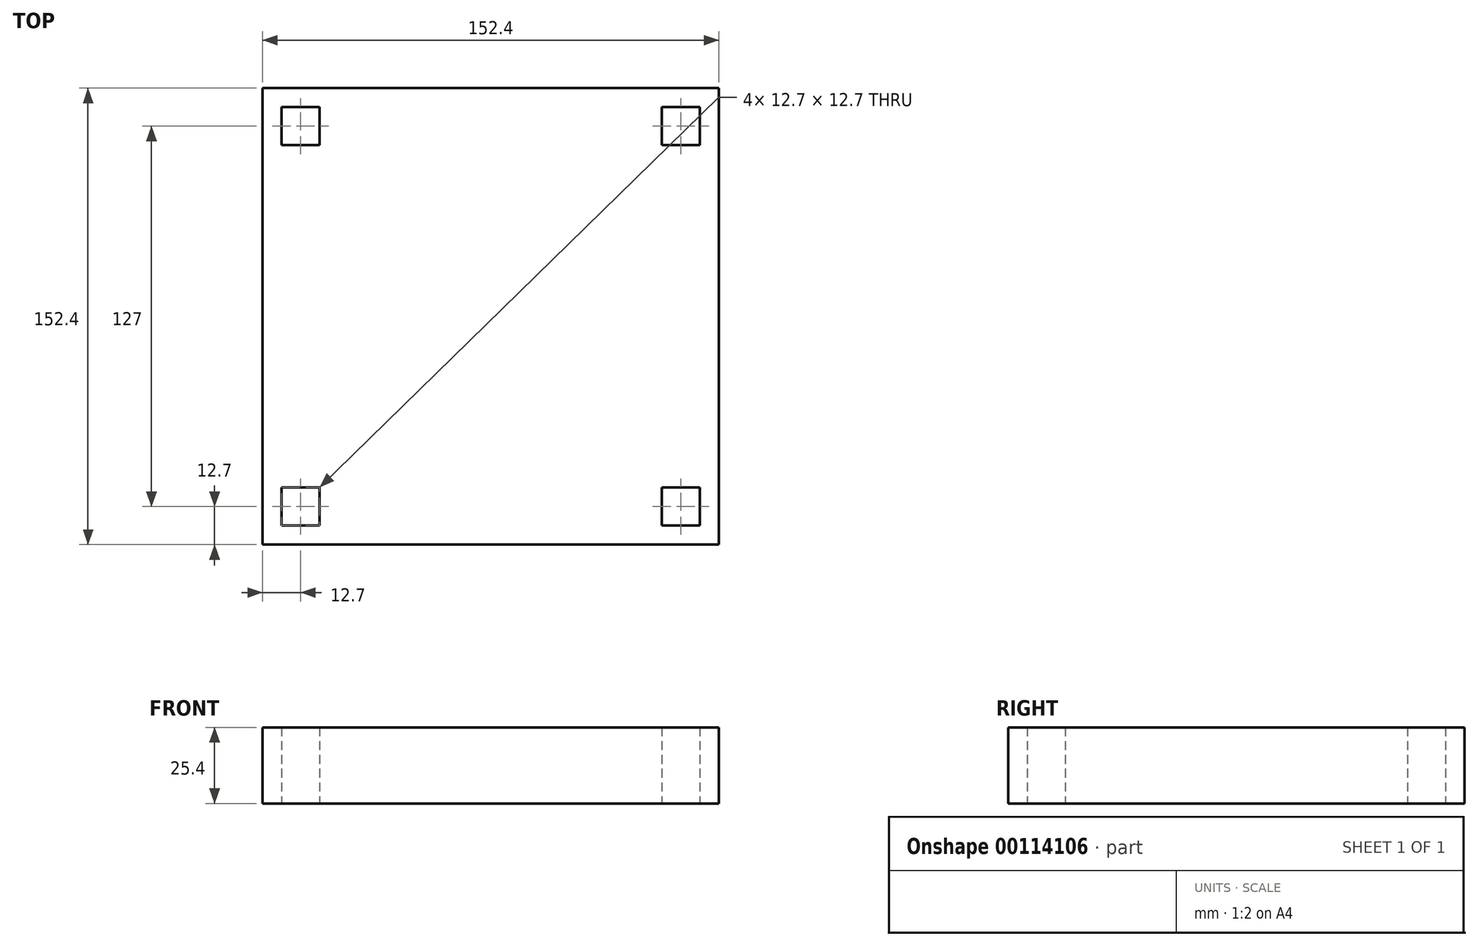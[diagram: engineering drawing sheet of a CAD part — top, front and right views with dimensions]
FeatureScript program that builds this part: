
annotation { "Feature Type Name" : "Feature", "Feature Type Description" : "" }
export const myFeature = defineFeature(function(context is Context, id is Id, definition is map)
    precondition{}
    {
        {
            var Q0;
            Q0=qCreatedBy(makeId("Top.planeOp"),FACE);
            var sketch = newSketch(context, id + "F0", { "sketchPlane" : qUnion([Q0])});
            skLineSegment(sketch, "E0.bottom", {"start": v(76.2, 76.2) * mm, "end": v(-76.2, 76.2) * mm});
            skLineSegment(sketch, "E0.top", {"start": v(76.2, -76.2) * mm, "end": v(-76.2, -76.2) * mm});
            skLineSegment(sketch, "E0.left", {"start": v(76.2, 76.2) * mm, "end": v(76.2, -76.2) * mm});
            skLineSegment(sketch, "E0.right", {"start": v(-76.2, 76.2) * mm, "end": v(-76.2, -76.2) * mm});
            skPoint(sketch, "E0.middle", {"position": v(0, 0) * mm});
            skLineSegment(sketch, "E1.bottom", {"start": v(-69.85, 69.85) * mm, "end": v(-57.15, 69.85) * mm});
            skLineSegment(sketch, "E1.top", {"start": v(-69.85, 57.15) * mm, "end": v(-57.15, 57.15) * mm});
            skLineSegment(sketch, "E1.left", {"start": v(-69.85, 69.85) * mm, "end": v(-69.85, 57.15) * mm});
            skLineSegment(sketch, "E1.right", {"start": v(-57.15, 69.85) * mm, "end": v(-57.15, 57.15) * mm});
            skLineSegment(sketch, "E2.MirrorCS", {"start": v(69.85, 57.15) * mm, "end": v(57.15, 57.15) * mm});
            skLineSegment(sketch, "E3.MirrorCS", {"start": v(69.85, 69.85) * mm, "end": v(69.85, 57.15) * mm});
            skLineSegment(sketch, "E4.MirrorCS", {"start": v(69.85, 69.85) * mm, "end": v(57.15, 69.85) * mm});
            skLineSegment(sketch, "E5.MirrorCS", {"start": v(57.15, 69.85) * mm, "end": v(57.15, 57.15) * mm});
            skLineSegment(sketch, "E6.MirrorCS", {"start": v(-69.85, -57.15) * mm, "end": v(-57.15, -57.15) * mm});
            skLineSegment(sketch, "E7.MirrorCS", {"start": v(-69.85, -69.85) * mm, "end": v(-69.85, -57.15) * mm});
            skLineSegment(sketch, "E8.MirrorCS", {"start": v(-69.85, -69.85) * mm, "end": v(-57.15, -69.85) * mm});
            skLineSegment(sketch, "E9.MirrorCS", {"start": v(-57.15, -69.85) * mm, "end": v(-57.15, -57.15) * mm});
            skLineSegment(sketch, "E10.MirrorCS", {"start": v(57.15, -69.85) * mm, "end": v(57.15, -57.15) * mm});
            skLineSegment(sketch, "E11.MirrorCS", {"start": v(69.85, -69.85) * mm, "end": v(57.15, -69.85) * mm});
            skLineSegment(sketch, "E12.MirrorCS", {"start": v(69.85, -69.85) * mm, "end": v(69.85, -57.15) * mm});
            skLineSegment(sketch, "E13.MirrorCS", {"start": v(69.85, -57.15) * mm, "end": v(57.15, -57.15) * mm});
            skSolve(sketch);
        }
        {
            var Q0;
            Q0 = qSketchRegion(id + "F0", true);
            extrude(context, id + "F1", {"entities" : qUnion([Q0]), "depth" : 25.4 * mm});
        }
    });
